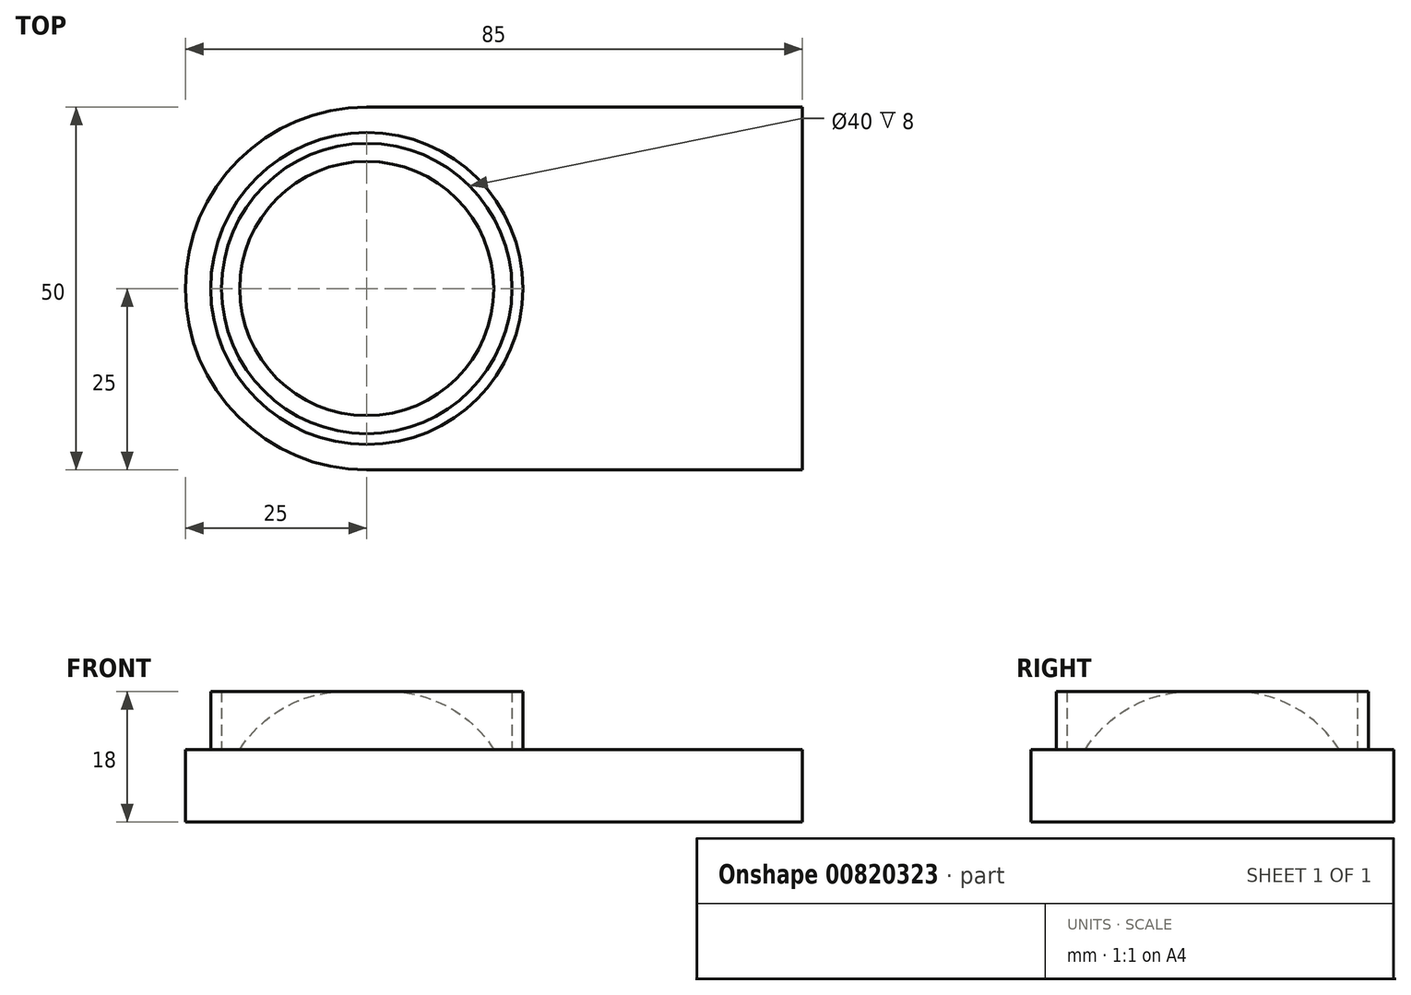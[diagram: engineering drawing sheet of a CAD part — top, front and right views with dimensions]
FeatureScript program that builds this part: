
annotation { "Feature Type Name" : "Feature", "Feature Type Description" : "" }
export const myFeature = defineFeature(function(context is Context, id is Id, definition is map)
    precondition{}
    {
        {
            var Q0;
            Q0=qCreatedBy(makeId("Top.planeOp"),FACE);
            var sketch = newSketch(context, id + "F0", { "sketchPlane" : qUnion([Q0])});
            skCircle(sketch, "E0", {"center": v(0, 0) * mm, "radius": 17.5 * mm});
            skCircle(sketch, "E1", {"center": v(0, 0) * mm, "radius": 20 * mm});
            skCircle(sketch, "E2", {"center": v(0, 0) * mm, "radius": 21.5 * mm});
            skArc(sketch, "E3", {"start": v(0, 25) * mm, "mid": v(-25, 0) * mm, "end": v(0, -25) * mm});
            skLineSegment(sketch, "E4", {"start": v(0, 25) * mm, "end": v(60, 25) * mm});
            skLineSegment(sketch, "E5", {"start": v(0, -25) * mm, "end": v(60, -25) * mm});
            skLineSegment(sketch, "E6", {"start": v(60, 25) * mm, "end": v(60, -25) * mm});
            skSolve(sketch);
        }
        {
            var Q0;
            Q0 = qSketchRegion(id + "F0", true);
            var Q1;
            Q1=makeQuery(id+"F0.imprint","IMPRINT",FACE,{"disambiguationData":[TD([[makeQuery(id+"F0.imprint","IMPRINT",EDGE,{"derivedFrom":sQuery(id+"F0.wireOp",EDGE,"E0")}),-1.0]])]});
            var Q2;
            Q2=makeQuery(id+"F0.imprint","IMPRINT",FACE,{"disambiguationData":[TD([[makeQuery(id+"F0.imprint","IMPRINT",EDGE,{"derivedFrom":sQuery(id+"F0.wireOp",EDGE,"E0")}),1.0]])]});
            var Q3;
            Q3=makeQuery(id+"F0.imprint","IMPRINT",FACE,{"disambiguationData":[TD([[makeQuery(id+"F0.imprint","IMPRINT",EDGE,{"derivedFrom":sQuery(id+"F0.wireOp",EDGE,"E1")}),-1.0]])]});
            extrude(context, id + "F1", {"entities" : qUnion([Q0, Q1, Q2, Q3]), "oppositeDirection" : true, "depth" : 10 * mm, "offsetDistance" : 25 * mm});
        }
        {
            var Q0;
            Q0=makeQuery(id+"F0.imprint","IMPRINT",FACE,{"disambiguationData":[TD([[makeQuery(id+"F0.imprint","IMPRINT",EDGE,{"derivedFrom":sQuery(id+"F0.wireOp",EDGE,"E1")}),-1.0]])]});
            extrude(context, id + "F2", {"entities" : qUnion([Q0]), "depth" : 8 * mm, "offsetDistance" : 25 * mm});
        }
        {
            var Q0;
            Q0=makeQuery(id+"F0.imprint","IMPRINT",FACE,{"disambiguationData":[TD([[makeQuery(id+"F0.imprint","IMPRINT",EDGE,{"derivedFrom":sQuery(id+"F0.wireOp",EDGE,"E0")}),1.0]])]});
            extrude(context, id + "F3", {"entities" : qUnion([Q0]), "depth" : 8 * mm, "offsetDistance" : 25 * mm});
        }
        {
            var Q0;
            Q0=makeQuery(id+"F3.opExtrude","CAP_EDGE",EDGE,{"disambiguationData":[OSD([sQuery(id+"F0.wireOp",EDGE,"E0")])],"isStart":false});
            fillet(context, id + "F4", {"entities" : qUnion([Q0]), "radius" : 17.5 * mm, "tangentPropagation" : true, "allowEdgeOverflow" : false});
        }
    });
